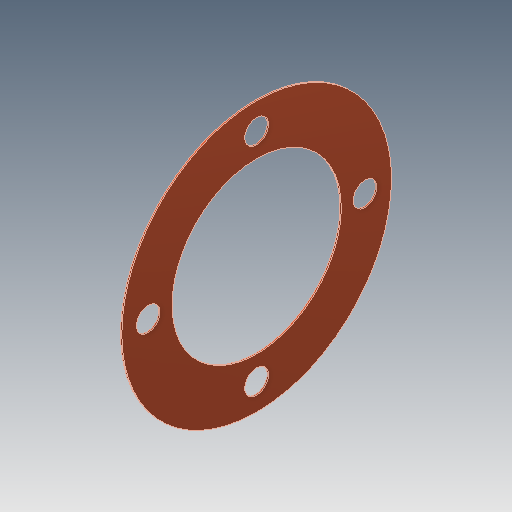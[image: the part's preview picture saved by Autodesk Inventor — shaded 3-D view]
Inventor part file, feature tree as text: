
AUTODESK INVENTOR PART (.ipt)
format: ipt  version: 2025 (Build 290162000, 162)  size: 102,912 bytes
history: native  units: in
note: dims shown in document units (in); Inventor stores cm internally (conversion verified against a paired STEP export)
features: sketch x2, extrude x1
ambient origin geometry x8: Origin, YZ Plane, XZ Plane, XY Plane, X Axis, Y Axis, Z Axis, Center Point
bodies: 实体1 (feature_tree)
feature tree (3):
  extrude  "拉伸1"  Depth=2.5197in
  sketch  "草图1"  dims[d0=0.3543in d2=2.5197in]
  sketch  "草图 - 环形阵列1"  dims[d1=4.0157in d3=2.5197in d4=0.3543in d5=1.6142in d6=1.5748in d8=360.0deg d10=0.0197in d11=0.0in]
